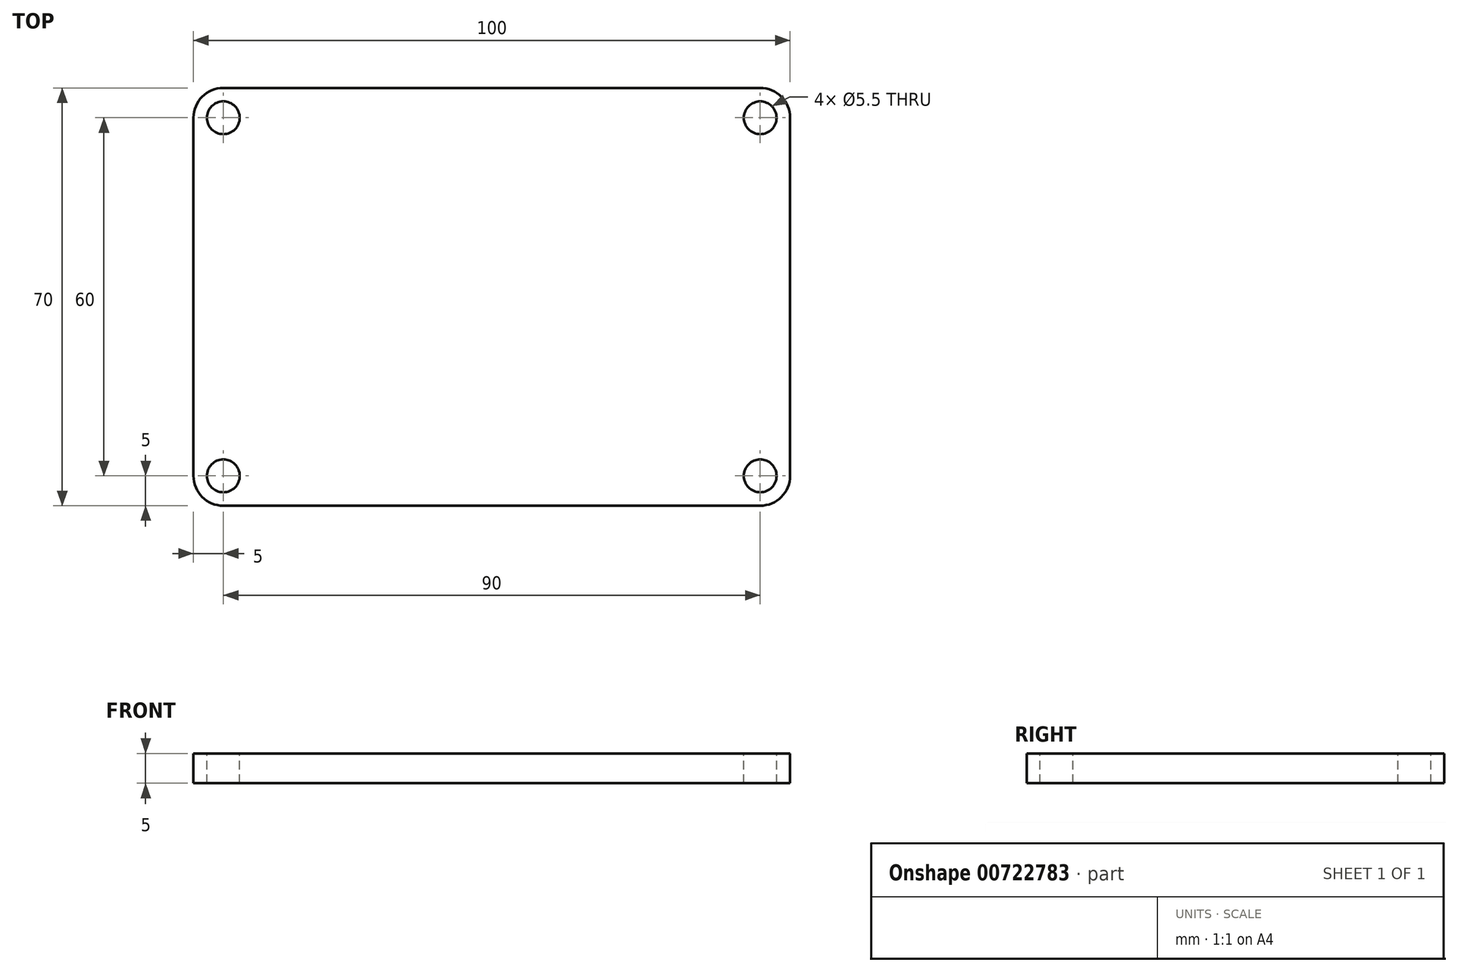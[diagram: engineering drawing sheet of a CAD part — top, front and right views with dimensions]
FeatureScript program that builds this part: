
annotation { "Feature Type Name" : "Feature", "Feature Type Description" : "" }
export const myFeature = defineFeature(function(context is Context, id is Id, definition is map)
    precondition{}
    {
        {
            var Q0;
            Q0=qCreatedBy(makeId("Top.planeOp"),FACE);
            var sketch = newSketch(context, id + "F0", { "sketchPlane" : qUnion([Q0])});
            skLineSegment(sketch, "E0.0.0", {"start": v(50, 35) * mm, "end": v(-50, 35) * mm});
            skLineSegment(sketch, "E0.0.1", {"start": v(-50, 35) * mm, "end": v(-50, -35) * mm});
            skLineSegment(sketch, "E0.0.2", {"start": v(-50, -35) * mm, "end": v(50, -35) * mm});
            skLineSegment(sketch, "E0.0.3", {"start": v(50, -35) * mm, "end": v(50, 35) * mm});
            skLineSegment(sketch, "E1.bottom", {"start": v(-45, 30) * mm, "end": v(45, 30) * mm});
            skLineSegment(sketch, "E1.top", {"start": v(-45, -30) * mm, "end": v(45, -30) * mm});
            skLineSegment(sketch, "E1.left", {"start": v(-45, 30) * mm, "end": v(-45, -30) * mm});
            skLineSegment(sketch, "E1.right", {"start": v(45, 30) * mm, "end": v(45, -30) * mm});
            skSolve(sketch);
        }
        {
            var Q0;
            Q0=makeQuery(id+"F0.imprint","IMPRINT",FACE,{"disambiguationData":[TD([[makeQuery(id+"F0.imprint","IMPRINT",EDGE,{"derivedFrom":sQuery(id+"F0.wireOp",EDGE,"E1.bottom")}),-1.0]])]});
            var Q1;
            Q1=makeQuery(id+"F0.imprint","IMPRINT",FACE,{"disambiguationData":[TD([[makeQuery(id+"F0.imprint","IMPRINT",EDGE,{"derivedFrom":sQuery(id+"F0.wireOp",EDGE,"E0.0.0")}),1.0]])]});
            extrude(context, id + "F1", {"entities" : qUnion([Q0, Q1]), "oppositeDirection" : true, "depth" : 5 * mm, "offsetDistance" : 25 * mm});
        }
        {
            var Q0;
            Q0=makeQuery(id+"F1.opExtrude","SWEPT_EDGE",EDGE,{"disambiguationData":[OSD([sQuery(id+"F0.wireOp",EDGE,"E0.0.1"),sQuery(id+"F0.wireOp",EDGE,"E0.0.2")])]});
            var Q1;
            Q1=makeQuery(id+"F1.opExtrude","SWEPT_EDGE",EDGE,{"disambiguationData":[OSD([sQuery(id+"F0.wireOp",EDGE,"E0.0.0"),sQuery(id+"F0.wireOp",EDGE,"E0.0.1")])]});
            var Q2;
            Q2=makeQuery(id+"F1.opExtrude","SWEPT_EDGE",EDGE,{"disambiguationData":[OSD([sQuery(id+"F0.wireOp",EDGE,"E0.0.2"),sQuery(id+"F0.wireOp",EDGE,"E0.0.3")])]});
            var Q3;
            Q3=makeQuery(id+"F1.opExtrude","SWEPT_EDGE",EDGE,{"disambiguationData":[OSD([sQuery(id+"F0.wireOp",EDGE,"E0.0.0"),sQuery(id+"F0.wireOp",EDGE,"E0.0.3")])]});
            fillet(context, id + "F2", {"entities" : qUnion([Q0, Q1, Q2, Q3]), "radius" : 5 * mm, "tangentPropagation" : true, "allowEdgeOverflow" : false});
        }
        {
            var Q0;
            Q0=makeQuery(id+"F1.opExtrude","CAP_FACE",FACE,{"disambiguationData":[OSD([sQuery(id+"F0.wireOp",EDGE,"E0.0.0"),sQuery(id+"F0.wireOp",EDGE,"E0.0.1"),sQuery(id+"F0.wireOp",EDGE,"E0.0.2"),sQuery(id+"F0.wireOp",EDGE,"E0.0.3")])],"isStart":true});
            var sketch = newSketch(context, id + "F3", { "sketchPlane" : qUnion([Q0])});
            skLineSegment(sketch, "E2.bottom", {"start": v(-45, 30) * mm, "end": v(45, 30) * mm});
            skLineSegment(sketch, "E2.top", {"start": v(-45, -30) * mm, "end": v(45, -30) * mm});
            skLineSegment(sketch, "E2.left", {"start": v(-45, 30) * mm, "end": v(-45, -30) * mm});
            skLineSegment(sketch, "E2.right", {"start": v(45, 30) * mm, "end": v(45, -30) * mm});
            skSolve(sketch);
        }
        {
            var Q0;
            Q0=sQuery(id+"F3.wireOp",VERTEX,"E2.left.start");
            var Q1;
            Q1=sQuery(id+"F3.wireOp",VERTEX,"E2.left.end");
            var Q2;
            Q2=sQuery(id+"F3.wireOp",VERTEX,"E2.top.end");
            var Q3;
            Q3=sQuery(id+"F3.wireOp",VERTEX,"E2.right.start");
            var Q4;
            Q4=makeQuery(id+"F1.opExtrude","SWEPT_BODY",BODY,{"disambiguationData":[OSD([sQuery(id+"F0.wireOp",EDGE,"E0.0.0"),sQuery(id+"F0.wireOp",EDGE,"E0.0.1"),sQuery(id+"F0.wireOp",EDGE,"E0.0.2"),sQuery(id+"F0.wireOp",EDGE,"E0.0.3")])]});
            hole(context, id + "F4", {"style" : HoleStyle.SIMPLE, "endStyle" : HoleEndStyle.THROUGH, "standardTappedOrClearance" : lookupTablePath({ "standard" : "ISO", "fit" : "Normal", "size" : "M5", "type" : "Clearance" }), "standardBlindInLast" : lookupTablePath({ "fit" : "Standard", "standard" : "ISO", "size" : "M5", "type" : "Clearance" }), "holeDiameter" : 5.5 * mm, "majorDiameter" : 5 * mm, "isTappedThrough" : true, "tappedDepth" : 12 * mm, "tapClearance" : 3, "locations" : qUnion([Q0, Q1, Q2, Q3]), "scope" : qUnion([Q4])});
        }
    });
